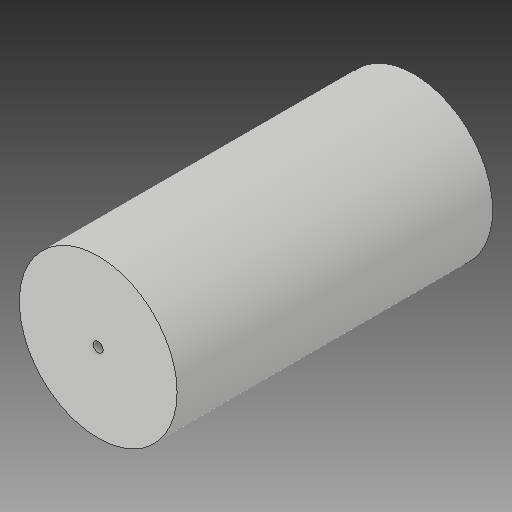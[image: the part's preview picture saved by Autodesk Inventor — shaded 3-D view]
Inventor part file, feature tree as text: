
AUTODESK INVENTOR PART (.ipt)
format: ipt  version: 2017 (Build 210142000, 142)  size: 93,184 bytes
history: native  units: in
note: dims shown in document units (in); Inventor stores cm internally (conversion verified against a paired STEP export)
features: extrude x1, hole x1, sketch x1
ambient origin geometry x8: Origin, YZ Plane, XZ Plane, XY Plane, X Axis, Y Axis, Z Axis, Center Point
bodies: Solid1 (feature_tree)
feature tree (3):
  extrude  "Extrusion1"  Depth=6.0in TaperAngle=0.0deg
  hole  "Hole1"  [1 undecoded]
  sketch  "Sketch1"  dims[d0=3.0in d1=6.0in d2=0.0in d3=1.0in d4=1.0in d5=0.188in d6=0.75in d7=0.375in d8=0.25in d9=0.5635in d10=1.0in d11=0.8108in]
note: 1 required parameter value undecoded (feature->parameter linkage not recoverable at this tier; creation-order binding heuristic only, values carry confidence <= 0.55)
